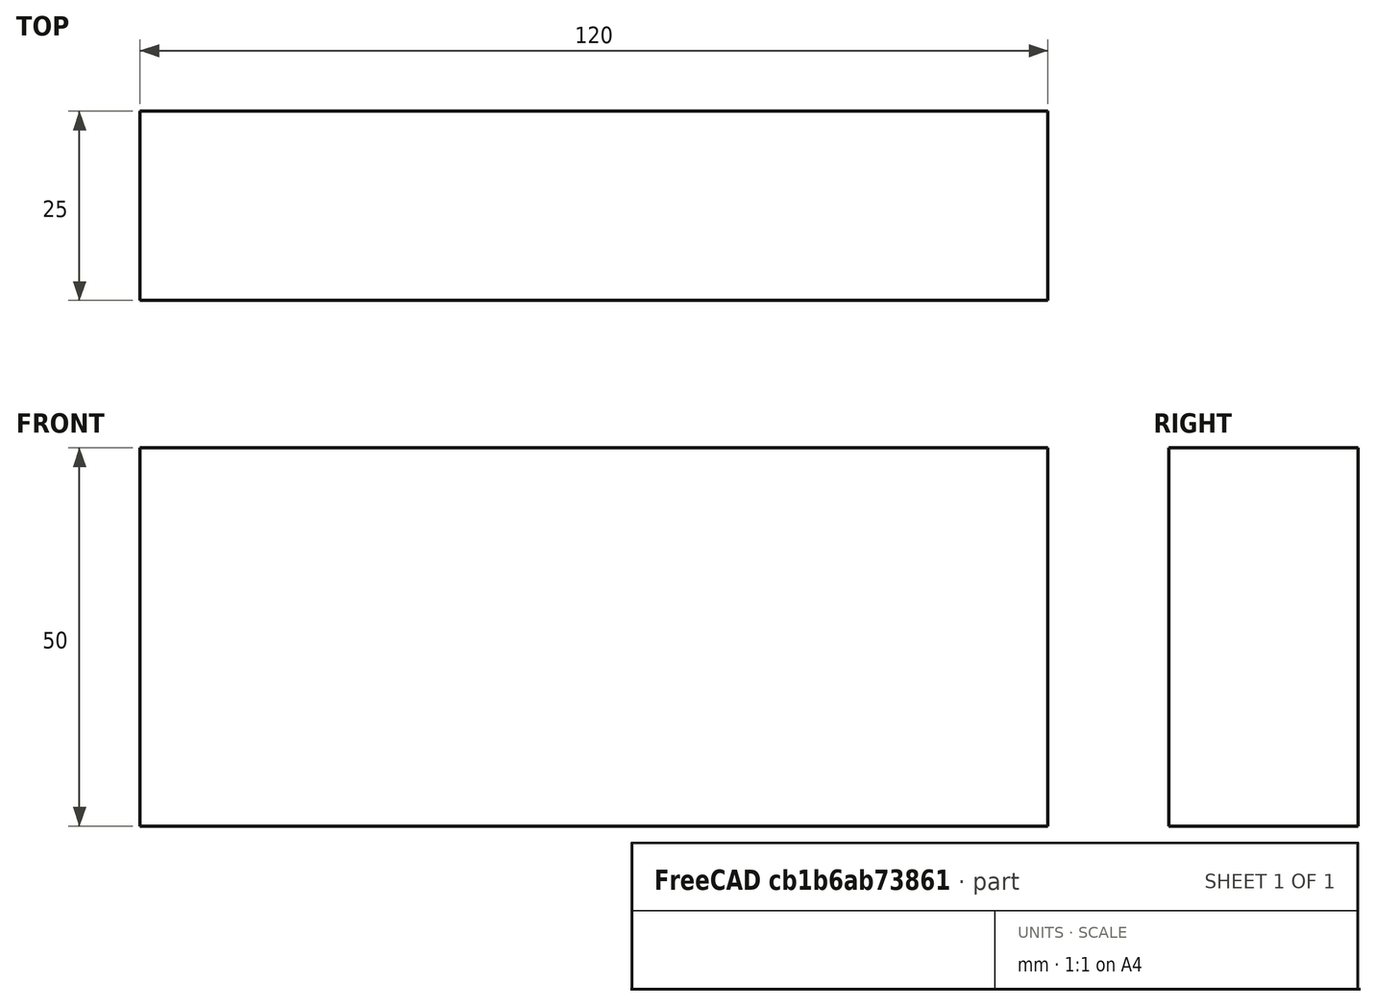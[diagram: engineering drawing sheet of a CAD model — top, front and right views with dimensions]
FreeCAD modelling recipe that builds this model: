
FCSTD DOCUMENT  (FreeCAD 0.15R4671 (Git))
Label: Flat Bar 120x25 EN10058 S235JR
License: All rights reserved
LicenseURL: http://en.wikipedia.org/wiki/All_rights_reserved
objects: Sketcher::SketchObject×1, Part::Extrusion×1
note: 2 computed .brp shape members not serialized (recipe doc carries the construction recipe); baked Part::Feature solids carry a one-line shape summary decoded from their .brp

FEATURE [Sketcher::SketchObject] Sketch
  sketch-geometry (4):
    g0: LineSegment StartX=-60 StartY=-12.5 StartZ=0 EndX=60 EndY=-12.5 EndZ=0
    g1: LineSegment StartX=60 StartY=-12.5 StartZ=0 EndX=60 EndY=12.5 EndZ=0
    g2: LineSegment StartX=60 StartY=12.5 StartZ=0 EndX=-60 EndY=12.5 EndZ=0
    g3: LineSegment StartX=-60 StartY=12.5 StartZ=0 EndX=-60 EndY=-12.5 EndZ=0
  constraints (12):
    c: Coincident(g0,g1)
    c: Coincident(g1,g2)
    c: Coincident(g2,g3)
    c: Coincident(g3,g0)
    c: Horizontal(g0)
    c: Horizontal(g2)
    c: Vertical(g1)
    c: Vertical(g3)
    c: Symmetric(g1,g2,g-2)
    c: Symmetric(g0,g1,g-1)
    c: DistanceY(g1) = 25
    c: DistanceX(g0) = 120
FEATURE [Part::Extrusion] Extrude  label="Flat Bar 120x25 EN10058 S235JR"
  Base = -> Sketch
  Dir = (0,0,50)
  Solid = true
